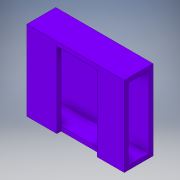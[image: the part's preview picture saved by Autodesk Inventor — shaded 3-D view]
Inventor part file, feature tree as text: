
AUTODESK INVENTOR PART (.ipt)
format: ipt  version: 2019 (Build 230136000, 136)  size: 146,432 bytes
history: native  units: mm
features: extrude x3, sketch x3, projected_geometry x3
ambient origin geometry x8: Origin, YZ Plane, XZ Plane, XY Plane, X Axis, Y Axis, Z Axis, Center Point
bodies: Solid1 (feature_tree)
feature tree (9):
  extrude  "Extrusion1"  Depth=15.0mm
  extrude  "Extrusion2"  Depth=72.18mm
  extrude  "Extrusion3"  Depth=20.0mm
  sketch  "Sketch1"  dims[d0=69.0mm d1=15.0mm]
  sketch  "Sketch2"  dims[d2=3.18mm d3=0.0mm d4=72.18mm]
  projected_geometry  "Projected Loop1"
  sketch  "Sketch3"  dims[d5=3.18mm d6=20.0mm d7=3.18mm d9=22.18mm d10=56.18mm d11=0.0mm d12=3.18mm d13=0.0mm]
  projected_geometry  "Projected Loop2"
  projected_geometry  "Projected Loop3"
